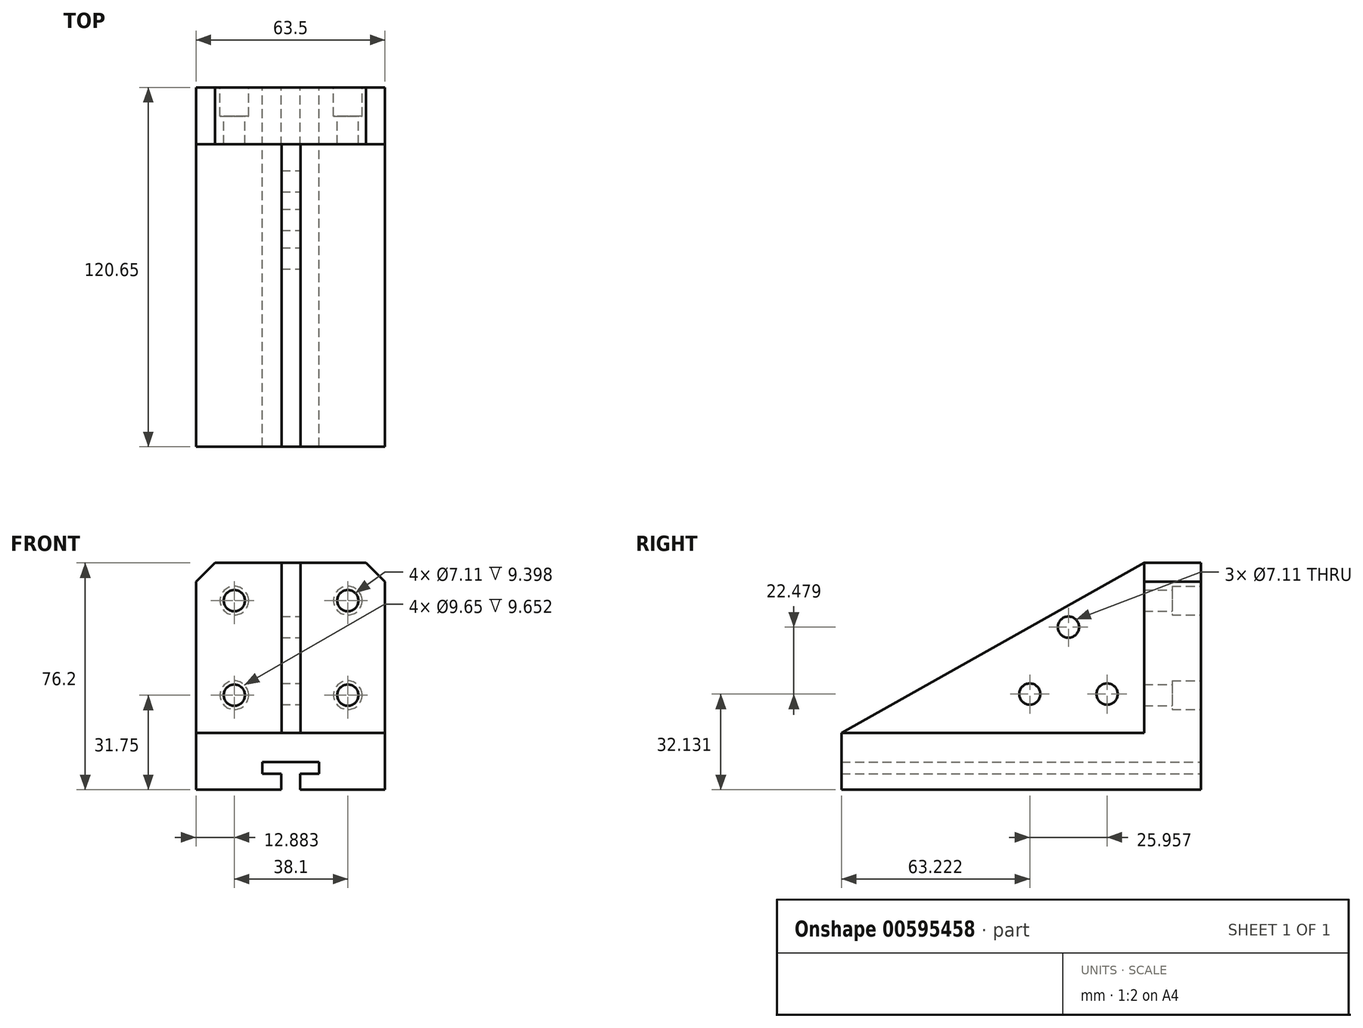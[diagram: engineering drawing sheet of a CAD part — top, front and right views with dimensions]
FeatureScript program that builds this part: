
annotation { "Feature Type Name" : "Feature", "Feature Type Description" : "" }
export const myFeature = defineFeature(function(context is Context, id is Id, definition is map)
    precondition{}
    {
        {
            var Q0;
            Q0=qCreatedBy(makeId("Front.planeOp"),FACE);
            var sketch = newSketch(context, id + "F0", { "sketchPlane" : qUnion([Q0])});
            skLineSegment(sketch, "E0", {"start": v(0, 69.85) * mm, "end": v(0, 0) * mm});
            skLineSegment(sketch, "E1", {"start": v(0, 0) * mm, "end": v(63.5, 0) * mm});
            skLineSegment(sketch, "E2", {"start": v(63.5, 0) * mm, "end": v(63.5, 69.85) * mm});
            skLineSegment(sketch, "E3", {"start": v(63.5, 69.85) * mm, "end": v(57.15, 76.2) * mm});
            skLineSegment(sketch, "E4", {"start": v(57.15, 76.2) * mm, "end": v(6.35, 76.2) * mm});
            skLineSegment(sketch, "E5", {"start": v(0, 69.85) * mm, "end": v(6.35, 76.2) * mm});
            skSolve(sketch);
        }
        {
            var Q0;
            Q0=makeQuery(id+"F0.imprint","IMPRINT",FACE,{"disambiguationData":[TD([[makeQuery(id+"F0.imprint","IMPRINT",EDGE,{"derivedFrom":sQuery(id+"F0.wireOp",EDGE,"E0")}),1.0]])]});
            extrude(context, id + "F1", {"entities" : qUnion([Q0]), "depth" : 19.05 * mm, "offsetDistance" : 25.4 * mm});
        }
        {
            var Q0;
            Q0=qCreatedBy(makeId("Front.planeOp"),FACE);
            var sketch = newSketch(context, id + "F2", { "sketchPlane" : qUnion([Q0])});
            skLineSegment(sketch, "E6", {"start": v(34.93, 0) * mm, "end": v(34.93, 5.38) * mm});
            skLineSegment(sketch, "E7", {"start": v(34.93, 5.38) * mm, "end": v(41.28, 5.38) * mm});
            skLineSegment(sketch, "E8", {"start": v(41.27, 5.38) * mm, "end": v(41.27, 9.35) * mm});
            skLineSegment(sketch, "E9", {"start": v(41.27, 9.35) * mm, "end": v(22.23, 9.35) * mm});
            skLineSegment(sketch, "E10", {"start": v(22.23, 9.35) * mm, "end": v(22.23, 5.38) * mm});
            skLineSegment(sketch, "E11", {"start": v(22.23, 5.38) * mm, "end": v(28.58, 5.38) * mm});
            skLineSegment(sketch, "E12", {"start": v(28.58, 5.38) * mm, "end": v(28.58, 0) * mm});
            skLineSegment(sketch, "E13", {"start": v(28.58, 0) * mm, "end": v(34.93, 0) * mm});
            skSolve(sketch);
        }
        {
            var Q0;
            Q0=qCreatedBy(makeId("Front.planeOp"),FACE);
            var sketch = newSketch(context, id + "F3", { "sketchPlane" : qUnion([Q0])});
            skLineSegment(sketch, "E14.bottom", {"start": v(0, 19.05) * mm, "end": v(63.5, 19.05) * mm});
            skLineSegment(sketch, "E14.top", {"start": v(0, 0) * mm, "end": v(63.5, 0) * mm});
            skLineSegment(sketch, "E14.left", {"start": v(0, 19.05) * mm, "end": v(0, 0) * mm});
            skLineSegment(sketch, "E14.right", {"start": v(63.5, 19.05) * mm, "end": v(63.5, 0) * mm});
            skSolve(sketch);
        }
        {
            var Q0;
            Q0 = qSketchRegion(id + "F3", true);
            extrude(context, id + "F4", {"entities" : qUnion([Q0]), "operationType" : NewBodyOperationType.ADD, "depth" : 120.65 * mm, "offsetDistance" : 25.4 * mm});
        }
        {
            var Q0;
            Q0 = qSketchRegion(id + "F2", true);
            extrude(context, id + "F5", {"entities" : qUnion([Q0]), "operationType" : NewBodyOperationType.REMOVE, "oppositeDirection" : true, "depth" : -120.65 * mm, "offsetDistance" : 25.4 * mm});
        }
        {
            var Q0;
            Q0=makeQuery(id+"F1.opExtrude","CAP_FACE",FACE,{"disambiguationData":[OSD([sQuery(id+"F0.wireOp",EDGE,"E0"),sQuery(id+"F0.wireOp",EDGE,"E1"),sQuery(id+"F0.wireOp",EDGE,"E2"),sQuery(id+"F0.wireOp",EDGE,"E3"),sQuery(id+"F0.wireOp",EDGE,"E4"),sQuery(id+"F0.wireOp",EDGE,"E5")])],"isStart":true});
            var sketch = newSketch(context, id + "F6", { "sketchPlane" : qUnion([Q0])});
            skCircle(sketch, "E15", {"center": v(-50.98, 31.75) * mm, "radius": 4.7 * mm});
            skCircle(sketch, "E16", {"center": v(-50.98, 63.5) * mm, "radius": 4.7 * mm});
            skCircle(sketch, "E17", {"center": v(-12.88, 63.5) * mm, "radius": 4.7 * mm});
            skCircle(sketch, "E18", {"center": v(-12.88, 31.75) * mm, "radius": 4.7 * mm});
            skSolve(sketch);
        }
        {
            var Q0;
            Q0=sQuery(id+"F6.wireOp",VERTEX,"E16.center");
            var Q1;
            Q1=sQuery(id+"F6.wireOp",VERTEX,"E17.center");
            var Q2;
            Q2=sQuery(id+"F6.wireOp",VERTEX,"E18.center");
            var Q3;
            Q3=sQuery(id+"F6.wireOp",VERTEX,"E15.center");
            var Q4;
            Q4=makeQuery(id+"F1.opExtrude","SWEPT_BODY",BODY,{"disambiguationData":[OSD([sQuery(id+"F0.wireOp",EDGE,"E0"),sQuery(id+"F0.wireOp",EDGE,"E1"),sQuery(id+"F0.wireOp",EDGE,"E2"),sQuery(id+"F0.wireOp",EDGE,"E3"),sQuery(id+"F0.wireOp",EDGE,"E4"),sQuery(id+"F0.wireOp",EDGE,"E5")])]});
            hole(context, id + "F7", {"style" : HoleStyle.C_BORE, "endStyle" : HoleEndStyle.THROUGH, "holeDiameter" : 7.11 * mm, "cBoreDiameter" : 9.65 * mm, "cBoreDepth" : 9.65 * mm, "majorDiameter" : 6.35 * mm, "isTappedThrough" : true, "tappedDepth" : 12.7 * mm, "tapClearance" : 3, "startFromSketch" : true, "locations" : qUnion([Q0, Q1, Q2, Q3]), "scope" : qUnion([Q4])});
        }
        {
            var Q0;
            Q0=qCreatedBy(makeId("Right.planeOp"),FACE);
            var sketch = newSketch(context, id + "F8", { "sketchPlane" : qUnion([Q0])});
            skLineSegment(sketch, "E19", {"start": v(-120.65, 19.05) * mm, "end": v(-19.05, 76.2) * mm});
            skLineSegment(sketch, "E20", {"start": v(-19.05, 76.2) * mm, "end": v(-19.05, 19.05) * mm});
            skLineSegment(sketch, "E21", {"start": v(-19.05, 19.05) * mm, "end": v(-120.65, 19.05) * mm});
            skSolve(sketch);
        }
        {
            var Q0;
            Q0 = qSketchRegion(id + "F8", true);
            extrude(context, id + "F9", {"entities" : qUnion([Q0]), "operationType" : NewBodyOperationType.ADD, "depth" : 35.05 * mm, "offsetDistance" : 25.4 * mm, "hasSecondDirection" : true, "secondDirectionOppositeDirection" : true, "secondDirectionDepth" : -28.7 * mm});
        }
        {
            var Q0;
            Q0=makeQuery(id+"F9.opExtrude","CAP_FACE",FACE,{"disambiguationData":[OSD([sQuery(id+"F8.wireOp",EDGE,"E19"),sQuery(id+"F8.wireOp",EDGE,"E20"),sQuery(id+"F8.wireOp",EDGE,"E21")])],"isStart":false});
            var sketch = newSketch(context, id + "F10", { "sketchPlane" : qUnion([Q0])});
            skCircle(sketch, "E22", {"center": v(-44.45, 39.62) * mm, "radius": 14.99 * mm});
            skCircle(sketch, "E23", {"center": v(-44.45, 54.61) * mm, "radius": 3.18 * mm});
            skCircle(sketch, "E24", {"center": v(-31.47, 32.13) * mm, "radius": 3.18 * mm});
            skCircle(sketch, "E25", {"center": v(-57.43, 32.13) * mm, "radius": 3.18 * mm});
            skLineSegment(sketch, "E26", {"start": v(-44.45, 39.62) * mm, "end": v(-57.43, 32.13) * mm});
            skLineSegment(sketch, "E27", {"start": v(-44.45, 39.62) * mm, "end": v(-44.45, 54.61) * mm});
            skSolve(sketch);
        }
        {
            var Q0;
            Q0=sQuery(id+"F10.wireOp",VERTEX,"E23.center");
            var Q1;
            Q1=sQuery(id+"F10.wireOp",VERTEX,"E24.center");
            var Q2;
            Q2=sQuery(id+"F10.wireOp",VERTEX,"E25.center");
            var Q3;
            Q3=makeQuery(id+"F1.opExtrude","SWEPT_BODY",BODY,{"disambiguationData":[OSD([sQuery(id+"F0.wireOp",EDGE,"E0"),sQuery(id+"F0.wireOp",EDGE,"E1"),sQuery(id+"F0.wireOp",EDGE,"E2"),sQuery(id+"F0.wireOp",EDGE,"E3"),sQuery(id+"F0.wireOp",EDGE,"E4"),sQuery(id+"F0.wireOp",EDGE,"E5")])]});
            hole(context, id + "F11", {"style" : HoleStyle.SIMPLE, "endStyle" : HoleEndStyle.BLIND, "holeDiameter" : 7.11 * mm, "majorDiameter" : 6.35 * mm, "holeDepth" : 12.7 * mm, "isTappedThrough" : true, "tappedDepth" : 12.7 * mm, "tapClearance" : 3, "startFromSketch" : true, "locations" : qUnion([Q0, Q1, Q2]), "scope" : qUnion([Q3])});
        }
    });
